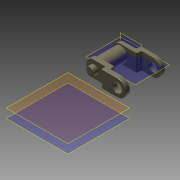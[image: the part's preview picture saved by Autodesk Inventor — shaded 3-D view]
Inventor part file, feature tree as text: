
AUTODESK INVENTOR PART (.ipt)
format: ipt  version: 2013 (Build 170138000, 138)  size: 276,480 bytes
history: native  units: in
note: dims shown in document units (in); Inventor stores cm internally (conversion verified against a paired STEP export)
features: plane x10, sketch x7, extrude x6, fillet x4, hole x1, mirror x1
ambient origin geometry x8: Origin, YZ Plane, XZ Plane, XY Plane, X Axis, Y Axis, Z Axis, Center Point
bodies: Solid1 (feature_tree)
feature tree (29):
  plane  "Work Plane1"
  extrude  "Extrusion2"  Depth=0.224in
  plane  "Work Plane2"
  extrude  "Extrusion4"  Depth=0.063in
  plane  "Work Plane3"
  extrude  "Extrusion7"  Depth=0.02in
  extrude  "Extrusion15"  Depth=0.1185in
  fillet  "Fillet5"  Radius=0.25in
  plane  "Work Plane9"
  plane  "Work Plane8"
  hole  "Hole2"  [1 undecoded]
  fillet  "Fillet13"  Radius=0.008in
  fillet  "Fillet14"  Radius=0.118in
  extrude  "Extrusion16"  Depth=0.0355in
  plane  "Work Plane10"
  extrude  "Extrusion17"  Depth=0.1215in TaperAngle=0.0deg
  fillet  "Fillet15"  Radius=0.008in
  mirror  "Mirror3"
  sketch  "Sketch2"  dims[d5=0.315in d6=0.0in d12=0.224in]
  sketch  "Sketch6"  dims[d15=0.059in d16=0.0in d17=0.063in]
  sketch  "Sketch10"  dims[d39=0.063in d40=0.059in d41=0.0in d42=0.0in d51=0.02in d52=0.02in]
  sketch  "Sketch18"  dims[d79=0.197in d82=0.1185in d87=0.25in d88=0.0in]
  sketch  "Sketch19"  dims[d89=0.02in]
  sketch  "Sketch20"  dims[d90=0.122in d91=0.75in d92=0.375in d93=0.25in d94=0.5635in d95=1.0in d96=0.8108in d97=0.008in d98=0.008in d99=0.118in]
  sketch  "Sketch21"  dims[d100=0.066in d101=0.0in d102=0.0355in d103=0.1215in d104=0.0in d105=0.008in]
  plane  "Work Plane11"
  plane  "Work Plane12"
  plane  "Work Plane13"
  plane  "Work Plane14"
note: 1 required parameter value undecoded (feature->parameter linkage not recoverable at this tier; creation-order binding heuristic only, values carry confidence <= 0.55)
